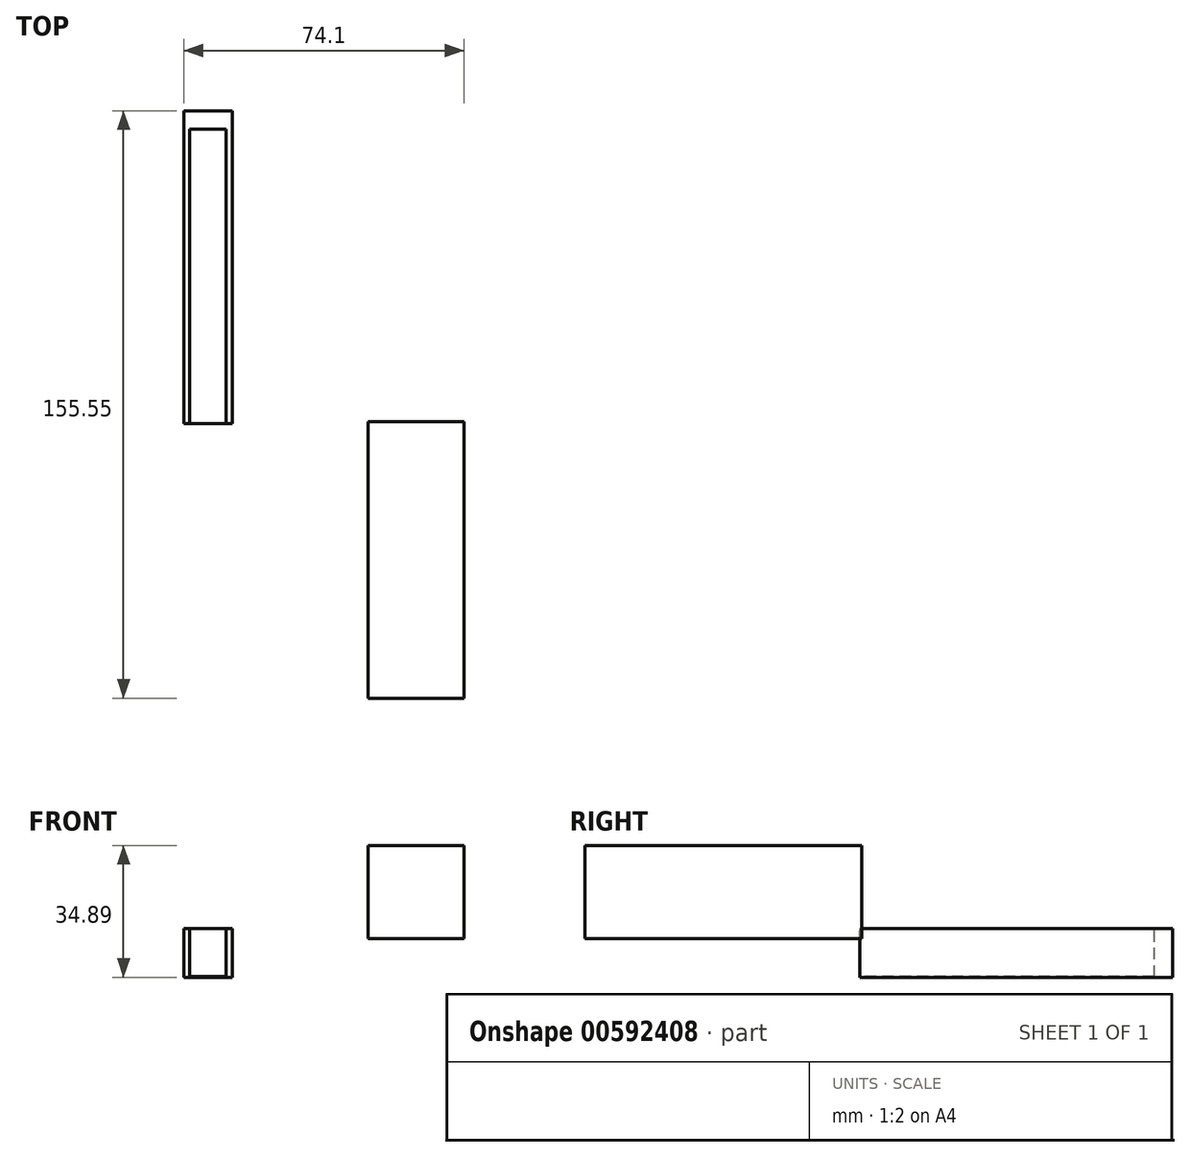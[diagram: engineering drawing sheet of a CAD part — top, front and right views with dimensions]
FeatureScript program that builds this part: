
annotation { "Feature Type Name" : "Feature", "Feature Type Description" : "" }
export const myFeature = defineFeature(function(context is Context, id is Id, definition is map)
    precondition{}
    {
        {
            var Q0;
            Q0=qCreatedBy(makeId("Front.planeOp"),FACE);
            var sketch = newSketch(context, id + "F0", { "sketchPlane" : qUnion([Q0])});
            skLineSegment(sketch, "E0.bottom", {"start": v(-48.7, 39.51) * mm, "end": v(-35.9, 39.51) * mm});
            skLineSegment(sketch, "E0.top", {"start": v(-48.7, 26.64) * mm, "end": v(-35.9, 26.64) * mm});
            skLineSegment(sketch, "E0.left", {"start": v(-48.7, 39.51) * mm, "end": v(-48.7, 26.64) * mm});
            skLineSegment(sketch, "E0.right", {"start": v(-35.9, 39.51) * mm, "end": v(-35.9, 26.64) * mm});
            skSolve(sketch);
        }
        {
            var Q0;
            Q0=makeQuery(id+"F0.imprint","IMPRINT",FACE,{"disambiguationData":[TD([[makeQuery(id+"F0.imprint","IMPRINT",EDGE,{"derivedFrom":sQuery(id+"F0.wireOp",EDGE,"E0.bottom")}),-1.0]])]});
            extrude(context, id + "F1", {"entities" : qUnion([Q0]), "depth" : 82.8 * mm, "offsetDistance" : 25.4 * mm});
        }
        {
            var Q0;
            Q0=makeQuery(id+"F1.opExtrude","SWEPT_FACE",FACE,{"disambiguationData":[OSD([sQuery(id+"F0.wireOp",EDGE,"E0.bottom")])]});
            var sketch = newSketch(context, id + "F2", { "sketchPlane" : qUnion([Q0])});
            skLineSegment(sketch, "E1.bottom", {"start": v(-47.22, -4.82) * mm, "end": v(-37.6, -4.82) * mm});
            skLineSegment(sketch, "E1.top", {"start": v(-47.22, -89.08) * mm, "end": v(-37.6, -89.08) * mm});
            skLineSegment(sketch, "E1.left", {"start": v(-47.22, -4.82) * mm, "end": v(-47.22, -89.08) * mm});
            skLineSegment(sketch, "E1.right", {"start": v(-37.6, -4.82) * mm, "end": v(-37.6, -89.08) * mm});
            skSolve(sketch);
        }
        {
            var Q0;
            {var subQ0=sQuery(id+"F2.wireOp",EDGE,"E1.bottom");Q0=makeQuery(id+"F2.imprint","IMPRINT",FACE,{"disambiguationData":[TD([[makeQuery(id+"F2.imprint","IMPRINT",EDGE,{"derivedFrom":subQ0}),-1.0]])]});}
            extrude(context, id + "F3", {"entities" : qUnion([Q0]), "operationType" : NewBodyOperationType.REMOVE, "oppositeDirection" : true, "depth" : 12.7 * mm, "offsetDistance" : 25.4 * mm});
        }
        {
            var Q0;
            Q0=qCreatedBy(makeId("Right.planeOp"),FACE);
            var sketch = newSketch(context, id + "F4", { "sketchPlane" : qUnion([Q0])});
            skLineSegment(sketch, "E2.bottom", {"start": v(-82.24, 61.53) * mm, "end": v(-155.55, 61.53) * mm});
            skLineSegment(sketch, "E2.top", {"start": v(-82.24, 36.87) * mm, "end": v(-155.55, 36.87) * mm});
            skLineSegment(sketch, "E2.left", {"start": v(-82.24, 61.53) * mm, "end": v(-82.24, 36.87) * mm});
            skLineSegment(sketch, "E2.right", {"start": v(-155.55, 61.53) * mm, "end": v(-155.55, 36.87) * mm});
            skSolve(sketch);
        }
        {
            var Q0;
            Q0=makeQuery(id+"F4.imprint","IMPRINT",FACE,{"disambiguationData":[TD([[makeQuery(id+"F4.imprint","IMPRINT",EDGE,{"derivedFrom":sQuery(id+"F4.wireOp",EDGE,"E2.bottom")}),1.0]])]});
            extrude(context, id + "F5", {"entities" : qUnion([Q0]), "depth" : 25.4 * mm, "offsetDistance" : 25.4 * mm});
        }
    });
